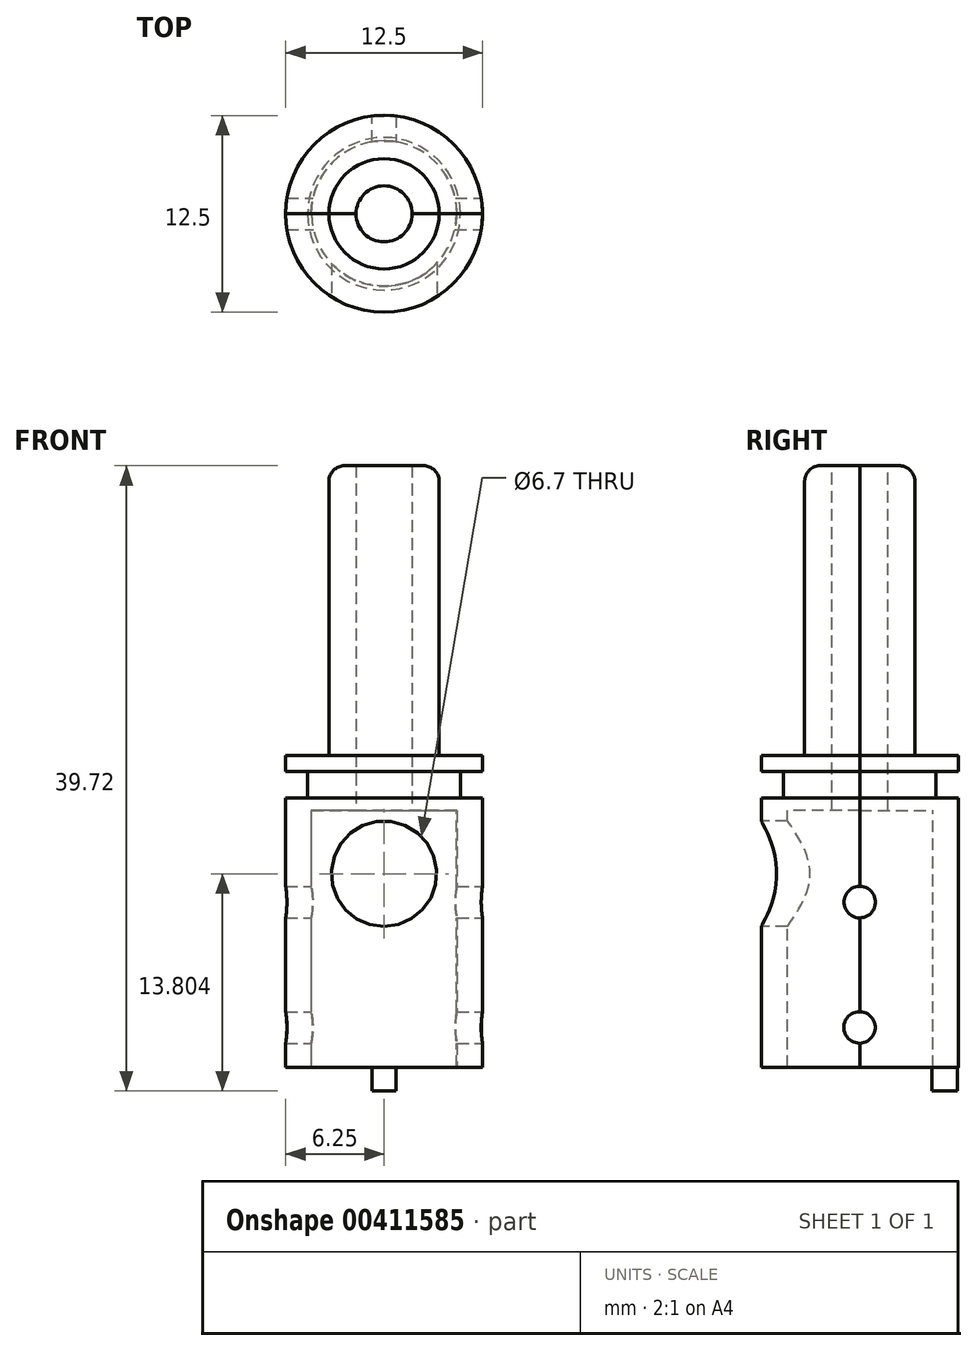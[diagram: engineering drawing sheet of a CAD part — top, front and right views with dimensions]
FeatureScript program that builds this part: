
annotation { "Feature Type Name" : "Feature", "Feature Type Description" : "" }
export const myFeature = defineFeature(function(context is Context, id is Id, definition is map)
    precondition{}
    {
        {
            var Q0;
            Q0=qCreatedBy(makeId("Right.planeOp"),FACE);
            var sketch = newSketch(context, id + "F0", { "sketchPlane" : qUnion([Q0])});
            skLineSegment(sketch, "E0", {"start": v(-14.78, 37.7) * mm, "end": v(-14.78, 19.28) * mm});
            skLineSegment(sketch, "E1", {"start": v(-14.78, 19.28) * mm, "end": v(-17.53, 19.28) * mm});
            skLineSegment(sketch, "E2", {"start": v(-17.53, 19.28) * mm, "end": v(-17.53, 18.28) * mm});
            skLineSegment(sketch, "E3", {"start": v(-17.53, 18.28) * mm, "end": v(-16.13, 18.28) * mm});
            skLineSegment(sketch, "E4", {"start": v(-16.13, 18.28) * mm, "end": v(-16.13, 16.58) * mm});
            skLineSegment(sketch, "E5", {"start": v(-16.13, 16.58) * mm, "end": v(-17.53, 16.58) * mm});
            skLineSegment(sketch, "E6", {"start": v(-17.53, 16.58) * mm, "end": v(-17.53, -0.52) * mm});
            skLineSegment(sketch, "E7", {"start": v(-17.53, -0.52) * mm, "end": v(-15.87, -0.52) * mm});
            skLineSegment(sketch, "E8", {"start": v(-15.87, -0.52) * mm, "end": v(-15.87, 15.8) * mm});
            skLineSegment(sketch, "E9", {"start": v(-6.64, 15.8) * mm, "end": v(-6.64, -0.52) * mm});
            skLineSegment(sketch, "E10", {"start": v(-6.64, -0.52) * mm, "end": v(-5.03, -0.52) * mm});
            skLineSegment(sketch, "E11", {"start": v(-5.03, -0.52) * mm, "end": v(-5.03, 16.58) * mm});
            skLineSegment(sketch, "E12", {"start": v(-5.03, 16.58) * mm, "end": v(-6.43, 16.58) * mm});
            skLineSegment(sketch, "E13", {"start": v(-6.43, 16.58) * mm, "end": v(-6.43, 18.28) * mm});
            skLineSegment(sketch, "E14", {"start": v(-6.43, 18.28) * mm, "end": v(-5.03, 18.28) * mm});
            skLineSegment(sketch, "E15", {"start": v(-5.03, 18.28) * mm, "end": v(-5.03, 19.28) * mm});
            skLineSegment(sketch, "E16", {"start": v(-5.03, 19.28) * mm, "end": v(-7.78, 19.28) * mm});
            skLineSegment(sketch, "E17", {"start": v(-7.78, 19.28) * mm, "end": v(-7.78, 37.7) * mm});
            skLineSegment(sketch, "E18", {"start": v(-13.06, 37.7) * mm, "end": v(-13.06, 15.8) * mm});
            skLineSegment(sketch, "E19", {"start": v(-9.5, 15.8) * mm, "end": v(-9.5, 37.7) * mm});
            skLineSegment(sketch, "E20", {"start": v(-15.87, 15.8) * mm, "end": v(-13.06, 15.8) * mm});
            skLineSegment(sketch, "E21", {"start": v(-9.5, 15.8) * mm, "end": v(-6.64, 15.8) * mm});
            skLineSegment(sketch, "E22", {"start": v(-9.5, 37.7) * mm, "end": v(-7.78, 37.7) * mm});
            skLineSegment(sketch, "E23", {"start": v(-13.06, 37.7) * mm, "end": v(-14.78, 37.7) * mm});
            skLineSegment(sketch, "E24", {"start": v(-11.28, 49.12) * mm, "end": v(-11.28, -7.35) * mm, "construction": true});
            skSolve(sketch);
        }
        {
            var Q0;
            Q0 = qSketchRegion(id + "F0", true);
            var Q1;
            Q1=sQuery(id+"F0.wireOp",EDGE,"E24");
            revolve(context, id + "F1", {"entities" : qUnion([Q0]), "axis" : qUnion([Q1]), "revolveType" : RevolveType.SYMMETRIC, "angle" : 180 * degree});
        }
        {
            var Q0;
            Q0=makeQuery(id+"F1.opRevolve","SWEPT_EDGE",EDGE,{"disambiguationData":[OSD([sQuery(id+"F0.wireOp",EDGE,"E17"),sQuery(id+"F0.wireOp",EDGE,"E22")])]});
            fillet(context, id + "F2", {"entities" : qUnion([Q0]), "radius" : 1 * mm, "tangentPropagation" : true, "allowEdgeOverflow" : false});
        }
        {
            var Q0;
            Q0=makeQuery(id+"F1.opRevolve","SWEPT_EDGE",EDGE,{"disambiguationData":[OSD([sQuery(id+"F0.wireOp",EDGE,"E0"),sQuery(id+"F0.wireOp",EDGE,"E23")])]});
            fillet(context, id + "F3", {"entities" : qUnion([Q0]), "radius" : 1 * mm, "tangentPropagation" : true, "allowEdgeOverflow" : false});
        }
        {
            var Q0;
            Q0=makeQuery(id+"F1.opRevolve","SWEPT_FACE",FACE,{"disambiguationData":[OSD([sQuery(id+"F0.wireOp",EDGE,"E10")])]});
            var sketch = newSketch(context, id + "F4", { "sketchPlane" : qUnion([Q0])});
            skLineSegment(sketch, "E25", {"start": v(-0.75, 6.7) * mm, "end": v(-0.75, 5.07) * mm});
            skLineSegment(sketch, "E26", {"start": v(-0.75, 5.07) * mm, "end": v(0.75, 5.07) * mm});
            skLineSegment(sketch, "E27", {"start": v(0.75, 5.07) * mm, "end": v(0.75, 6.7) * mm});
            skLineSegment(sketch, "E28", {"start": v(0.75, 6.7) * mm, "end": v(-0.75, 6.7) * mm});
            skSolve(sketch);
        }
        {
            var Q0;
            Q0 = qSketchRegion(id + "F4", true);
            extrude(context, id + "F5", {"entities" : qUnion([Q0]), "operationType" : NewBodyOperationType.ADD, "depth" : 1.5 * mm});
        }
        {
            var Q0;
            Q0=qCreatedBy(makeId("Front.planeOp"),FACE);
            cPlane(context, id + "F6", {"entities" : qUnion([Q0]), "cplaneType" : CPlaneType.OFFSET, "offset" : 20.2 * mm, "width" : 150 * mm, "height" : 150 * mm});
        }
        {
            var Q0;
            Q0=qCreatedBy(id+"F6.planeOp",FACE);
            var sketch = newSketch(context, id + "F7", { "sketchPlane" : qUnion([Q0])});
            skCircle(sketch, "E29", {"center": v(0, 11.78) * mm, "radius": 3.75 * mm});
            skSolve(sketch);
        }
        {
            var Q0;
            Q0=sQuery(id+"F7.wireOp",VERTEX,"E29.center");
            var Q1;
            Q1=makeQuery(id+"F1.opRevolve","SWEPT_BODY",BODY,{"disambiguationData":[OSD([sQuery(id+"F0.wireOp",EDGE,"E0"),sQuery(id+"F0.wireOp",EDGE,"E1"),sQuery(id+"F0.wireOp",EDGE,"E2"),sQuery(id+"F0.wireOp",EDGE,"E3"),sQuery(id+"F0.wireOp",EDGE,"E4"),sQuery(id+"F0.wireOp",EDGE,"E5"),sQuery(id+"F0.wireOp",EDGE,"E6"),sQuery(id+"F0.wireOp",EDGE,"E7"),sQuery(id+"F0.wireOp",EDGE,"E8"),sQuery(id+"F0.wireOp",EDGE,"E18"),sQuery(id+"F0.wireOp",EDGE,"E20"),sQuery(id+"F0.wireOp",EDGE,"E23")])]});
            hole(context, id + "F8", {"style" : HoleStyle.SIMPLE, "endStyle" : HoleEndStyle.BLIND, "holeDiameter" : 6.7 * mm, "holeDepth" : 5 * mm, "isTappedThrough" : true, "tappedDepth" : 12 * mm, "tapClearance" : 3, "locations" : qUnion([Q0]), "scope" : qUnion([Q1])});
        }
        {
            var Q0;
            Q0=qCreatedBy(makeId("Right.planeOp"),FACE);
            cPlane(context, id + "F9", {"entities" : qUnion([Q0]), "cplaneType" : CPlaneType.OFFSET, "offset" : 7.4 * mm, "width" : 150 * mm, "height" : 150 * mm});
        }
        {
            var Q0;
            Q0=qCreatedBy(id+"F9.planeOp",FACE);
            var sketch = newSketch(context, id + "F10", { "sketchPlane" : qUnion([Q0])});
            skPoint(sketch, "E30", {"position": v(-11.3, 2.02) * mm});
            skCircle(sketch, "E31", {"center": v(-11.3, 2.02) * mm, "radius": 1 * mm});
            skPoint(sketch, "E32", {"position": v(-11.28, 9.98) * mm});
            skCircle(sketch, "E33", {"center": v(-11.28, 9.98) * mm, "radius": 1 * mm});
            skSolve(sketch);
        }
        {
            var Q0;
            Q0=sQuery(id+"F10.wireOp",VERTEX,"E32");
            var Q1;
            Q1=makeQuery(id+"F1.opRevolve","SWEPT_BODY",BODY,{"disambiguationData":[OSD([sQuery(id+"F0.wireOp",EDGE,"E9"),sQuery(id+"F0.wireOp",EDGE,"E10"),sQuery(id+"F0.wireOp",EDGE,"E11"),sQuery(id+"F0.wireOp",EDGE,"E12"),sQuery(id+"F0.wireOp",EDGE,"E13"),sQuery(id+"F0.wireOp",EDGE,"E14"),sQuery(id+"F0.wireOp",EDGE,"E15"),sQuery(id+"F0.wireOp",EDGE,"E16"),sQuery(id+"F0.wireOp",EDGE,"E17"),sQuery(id+"F0.wireOp",EDGE,"E19"),sQuery(id+"F0.wireOp",EDGE,"E21"),sQuery(id+"F0.wireOp",EDGE,"E22")])]});
            var Q2;
            Q2=makeQuery(id+"F1.opRevolve","SWEPT_BODY",BODY,{"disambiguationData":[OSD([sQuery(id+"F0.wireOp",EDGE,"E0"),sQuery(id+"F0.wireOp",EDGE,"E1"),sQuery(id+"F0.wireOp",EDGE,"E2"),sQuery(id+"F0.wireOp",EDGE,"E3"),sQuery(id+"F0.wireOp",EDGE,"E4"),sQuery(id+"F0.wireOp",EDGE,"E5"),sQuery(id+"F0.wireOp",EDGE,"E6"),sQuery(id+"F0.wireOp",EDGE,"E7"),sQuery(id+"F0.wireOp",EDGE,"E8"),sQuery(id+"F0.wireOp",EDGE,"E18"),sQuery(id+"F0.wireOp",EDGE,"E20"),sQuery(id+"F0.wireOp",EDGE,"E23")])]});
            hole(context, id + "F11", {"style" : HoleStyle.SIMPLE, "endStyle" : HoleEndStyle.THROUGH, "holeDiameter" : 2 * mm, "isTappedThrough" : true, "tappedDepth" : 12 * mm, "tapClearance" : 3, "locations" : qUnion([Q0]), "scope" : qUnion([Q1, Q2])});
        }
        {
            var Q0;
            Q0=sQuery(id+"F10.wireOp",VERTEX,"E30");
            var Q1;
            Q1=makeQuery(id+"F1.opRevolve","SWEPT_BODY",BODY,{"disambiguationData":[OSD([sQuery(id+"F0.wireOp",EDGE,"E9"),sQuery(id+"F0.wireOp",EDGE,"E10"),sQuery(id+"F0.wireOp",EDGE,"E11"),sQuery(id+"F0.wireOp",EDGE,"E12"),sQuery(id+"F0.wireOp",EDGE,"E13"),sQuery(id+"F0.wireOp",EDGE,"E14"),sQuery(id+"F0.wireOp",EDGE,"E15"),sQuery(id+"F0.wireOp",EDGE,"E16"),sQuery(id+"F0.wireOp",EDGE,"E17"),sQuery(id+"F0.wireOp",EDGE,"E19"),sQuery(id+"F0.wireOp",EDGE,"E21"),sQuery(id+"F0.wireOp",EDGE,"E22")])]});
            var Q2;
            Q2=makeQuery(id+"F1.opRevolve","SWEPT_BODY",BODY,{"disambiguationData":[OSD([sQuery(id+"F0.wireOp",EDGE,"E0"),sQuery(id+"F0.wireOp",EDGE,"E1"),sQuery(id+"F0.wireOp",EDGE,"E2"),sQuery(id+"F0.wireOp",EDGE,"E3"),sQuery(id+"F0.wireOp",EDGE,"E4"),sQuery(id+"F0.wireOp",EDGE,"E5"),sQuery(id+"F0.wireOp",EDGE,"E6"),sQuery(id+"F0.wireOp",EDGE,"E7"),sQuery(id+"F0.wireOp",EDGE,"E8"),sQuery(id+"F0.wireOp",EDGE,"E18"),sQuery(id+"F0.wireOp",EDGE,"E20"),sQuery(id+"F0.wireOp",EDGE,"E23")])]});
            hole(context, id + "F12", {"style" : HoleStyle.SIMPLE, "endStyle" : HoleEndStyle.THROUGH, "holeDiameter" : 2 * mm, "isTappedThrough" : true, "tappedDepth" : 12 * mm, "tapClearance" : 3, "locations" : qUnion([Q0]), "scope" : qUnion([Q1, Q2])});
        }
    });
